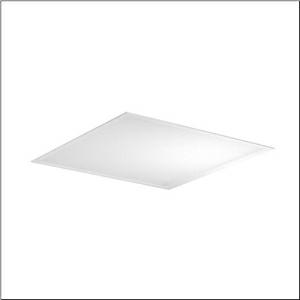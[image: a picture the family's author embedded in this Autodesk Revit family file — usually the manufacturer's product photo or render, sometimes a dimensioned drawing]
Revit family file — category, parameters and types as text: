
# Revit family: apollon_21_square_51mq12w72414
name_source: partatom
category: Lighting Fixtures
units: mm (PartAtom-declared; Revit-internal decimal feet)

## family parameters
Cut with Voids When Loaded = No
Host = Face
Light Source = No
Part Type = Normal
Room Calculation Point = No
Round Connector Dimension = Use Diameter
Shared = No

## types (1)
- Apollon 21 square (1 x LED, 4200 lm, 23.3 W, 4000K)
    Apparent Load = 23 VA
    CIE Flux Codes = 60 87 97 100 100
    Color Rendering = 80
    Color Temperature = 4000K
    Default Elevation = 1800 mm
    Description = Apollon 21 square, office luminaire, primary optical cover: micro prismatic cover, of PMMA, CAT 2 (L<= 3000cd/m²), light emission: direct distribution, primary light characteristic: symmetric, installation type: lay-in mounting, LED, rated luminous flux: 4.200lm, luminous efficacy: 180lm/W, light colour: 840, colour temperature: 4000K, control gear: ON/OFF, with terminal, 3-pole, mains connection: 220..240V, AC/DC, 0/50..60Hz, rated input power: 23W, housing, of aluminium, coated, traffic white (RAL 9016), module: M600, length: 595mm, width: 595mm, height: 55mm, recess depth: 180mm, housing upper side, of sheet steel, galvanised, protection rating (complete): IP20, protection rating (lamp compartment, on room side): IP50, insulation class (complete): insulation class II (safety insulation), certification: CE, ENEC, impact resistance: IK03, permissible operating ambient temperature: -20..+45°C, permissible storage temperature: -40..+80°C, standard: EN 60598-2-22, packaging unit: 1 piece
    Height = 0 mm  [stored 0 ft]
    Lamp = 1 x LED
    Lamp Light Flux = 4200 lm
    Lamp Power = 23.3 W
    Lamp count = 1
    Length = 595 mm
    Luminous efficacy = 180 lm/W
    Manufacturer = Siteco
    ModVariant = No
    Model = 51MQ12W72414
    Mounting Place = Ceiling
    Mounting Type = Recessed
    Number of Poles = 1
    OnlyDefault = Yes
    Power Factor = 1
    Product Name = Apollon 21 square
    Product group = office luminaire | ceiling recessed
    ProductGroupID = 401
    Protection Class = Protection class II
    Protection Degree = IP 20
    RLX_Detail_Level = 1
    RLX_Emergency_Light_Flux = 0 lm
    RLX_Emergency_Type = 0
    RLX_Emergency_Type_DB = No
    RlxData = <blob elided: 12549 chars, md5=9e2af732>
    Socket = socket
    Standby Power = 0 W
    System Light Flux = 4200 lm
    System Power = 23 W
    Type Comments = Product without accessories
    Type Image = l_1291049.jpg
    URL = http://relux.com
    VarID = ---
    Voltage = 0 V
    Weight = 0.00 kg
    Width = 595 mm

note: [stored X ft] marks values corroborated as IEEE doubles in the binary element streams (Revit-internal decimal feet)

## geometry (parser evidence)
native form markers: Sweep x10
no freeform markers — native parametric forms only
